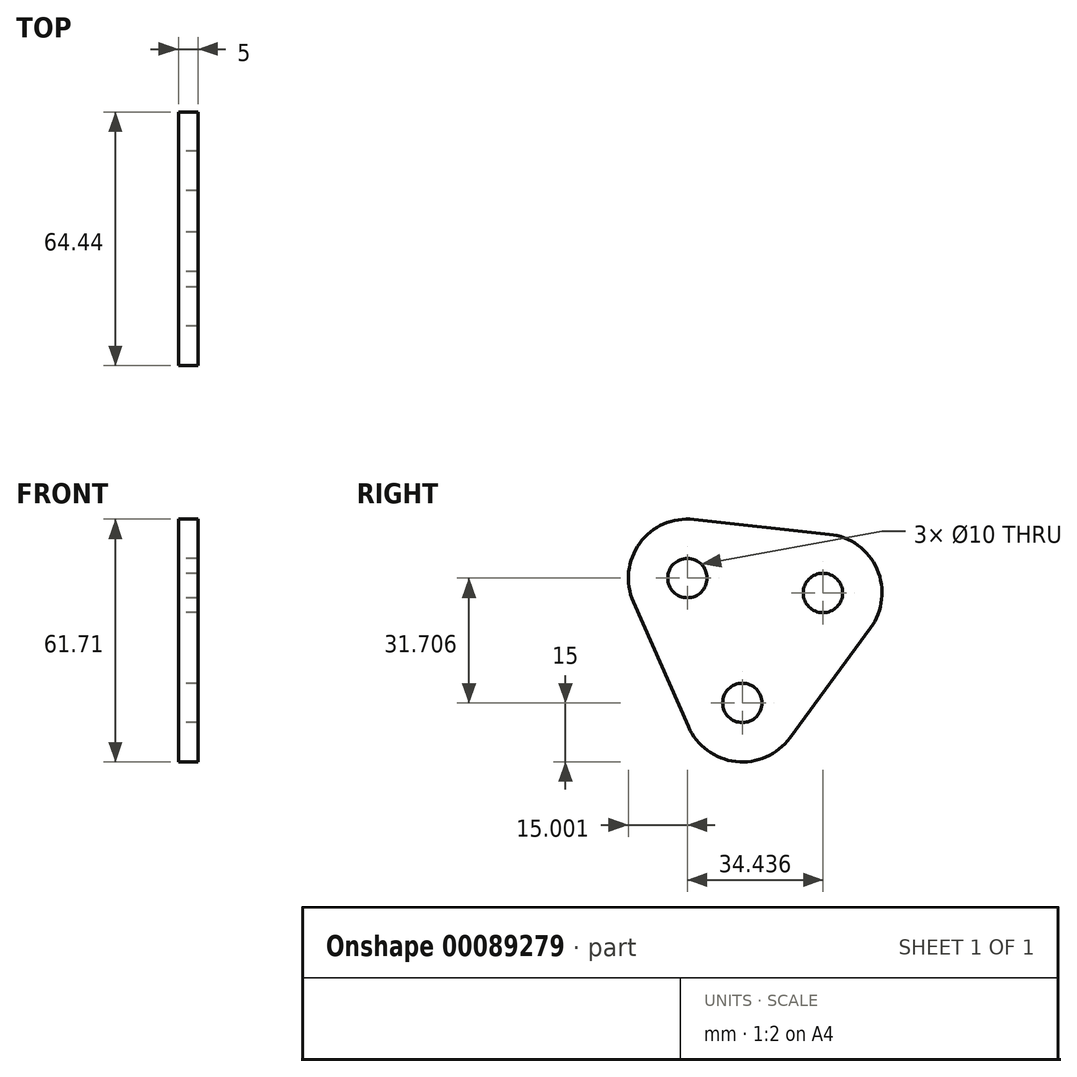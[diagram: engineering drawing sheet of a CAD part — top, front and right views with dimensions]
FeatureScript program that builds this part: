
annotation { "Feature Type Name" : "Feature", "Feature Type Description" : "" }
export const myFeature = defineFeature(function(context is Context, id is Id, definition is map)
    precondition{}
    {
        {
            var Q0;
            Q0=qCreatedBy(makeId("Right.planeOp"),FACE);
            var sketch = newSketch(context, id + "F0", { "sketchPlane" : qUnion([Q0])});
            skCircle(sketch, "E0.cCircle", {"center": v(0, 0) * mm, "radius": 20 * mm, "construction": true});
            skPoint(sketch, "E0.0.midPoint", {"position": v(18.3, 8.05) * mm});
            skCircle(sketch, "E1", {"center": v(18.3, 8.05) * mm, "radius": 5 * mm});
            skArc(sketch, "E2", {"start": v(30.4, -0.82) * mm, "mid": v(32.04, 14.1) * mm, "end": v(19.94, 22.96) * mm});
            skCircle(sketch, "E3", {"center": v(-2.18, -19.88) * mm, "radius": 5 * mm});
            skCircle(sketch, "E4", {"center": v(-16.13, 11.83) * mm, "radius": 5 * mm});
            skArc(sketch, "E5", {"start": v(-14.5, 26.74) * mm, "mid": v(-28.22, 20.7) * mm, "end": v(-29.86, 5.79) * mm});
            skArc(sketch, "E6", {"start": v(-15.91, -25.92) * mm, "mid": v(-3.82, -34.8) * mm, "end": v(9.91, -28.75) * mm});
            skLineSegment(sketch, "E7", {"start": v(-14.5, 26.74) * mm, "end": v(19.94, 22.96) * mm});
            skLineSegment(sketch, "E8", {"start": v(30.4, -0.82) * mm, "end": v(9.91, -28.75) * mm});
            skLineSegment(sketch, "E9", {"start": v(-29.86, 5.79) * mm, "end": v(-15.91, -25.92) * mm});
            skSolve(sketch);
        }
        {
            var Q0;
            Q0 = qSketchRegion(id + "F0", true);
            extrude(context, id + "F1", {"entities" : qUnion([Q0]), "depth" : 5 * mm});
        }
    });
